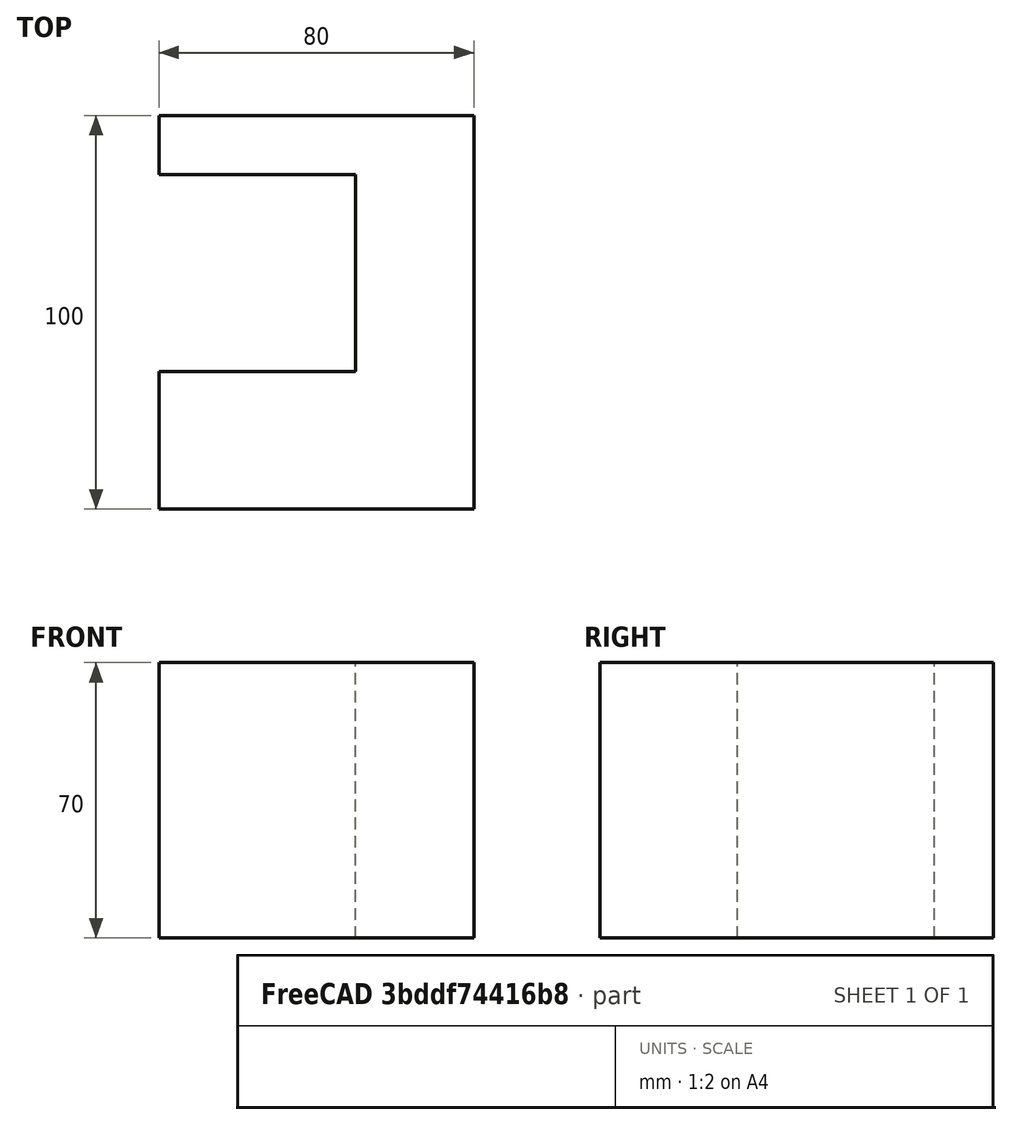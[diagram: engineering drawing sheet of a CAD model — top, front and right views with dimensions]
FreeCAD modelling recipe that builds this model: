
FCSTD DOCUMENT  (FreeCAD 0.19R22960 (Git))
Label: filament-halter
License: All rights reserved
LicenseURL: http://en.wikipedia.org/wiki/All_rights_reserved
objects: Sketcher::SketchObject×1, PartDesign::Pad×1, PartDesign::Body×1
note: 4 computed .brp shape members not serialized (recipe doc carries the construction recipe); baked Part::Feature solids carry a one-line shape summary decoded from their .brp

FEATURE [Sketcher::SketchObject] Sketch
  MapMode = 5
  Support = -> [XY_Plane]
  sketch-geometry (8):
    g0: LineSegment StartX=-60.4839 StartY=51.1694 StartZ=0 EndX=19.5161 EndY=51.1694 EndZ=0
    g1: LineSegment StartX=19.5161 StartY=51.1694 StartZ=0 EndX=19.5161 EndY=-48.8306 EndZ=0
    g2: LineSegment StartX=19.5161 StartY=-48.8306 StartZ=0 EndX=-60.4839 EndY=-48.8306 EndZ=0
    g3: LineSegment StartX=-60.4839 StartY=-48.8306 StartZ=0 EndX=-60.4839 EndY=-13.8306 EndZ=0
    g4: LineSegment StartX=-60.4839 StartY=-13.8306 StartZ=0 EndX=-10.4839 EndY=-13.8306 EndZ=0
    g5: LineSegment StartX=-10.4839 StartY=-13.8306 StartZ=0 EndX=-10.4839 EndY=36.1694 EndZ=0
    g6: LineSegment StartX=-10.4839 StartY=36.1694 StartZ=0 EndX=-60.4839 EndY=36.1694 EndZ=0
    g7: LineSegment StartX=-60.4839 StartY=36.1694 StartZ=0 EndX=-60.4839 EndY=51.1694 EndZ=0
  constraints (22):
    c: Horizontal(g0)
    c: Coincident(g0,g1)
    c: Coincident(g1,g2)
    c: Horizontal(g2)
    c: Coincident(g2,g3)
    c: Vertical(g3)
    c: Coincident(g3,g4)
    c: Horizontal(g4)
    c: Coincident(g4,g5)
    c: Vertical(g5)
    c: Coincident(g5,g6)
    c: Horizontal(g6)
    c: Coincident(g6,g7)
    c: Coincident(g7,g0)
    c: Vertical(g7)
    c: DistanceY(g7,g7) = 15
    c: DistanceX(g0,g0) = 80
    c: Vertical(g1)
    c: Equal(g0,g2)
    c: DistanceY(g5,g5) = 50
    c: DistanceY(g3,g3) = 35
    c: DistanceX(g6,g6) = 50
FEATURE [PartDesign::Pad] Pad
  Direction = (1,1,1)
  Length = 70
  Length2 = 100
  Profile = -> Sketch
  Type = 0
FEATURE [PartDesign::Body] Body
  Group = -> [Sketch,Pad]
  Origin = -> Origin
  Tip = -> Pad
